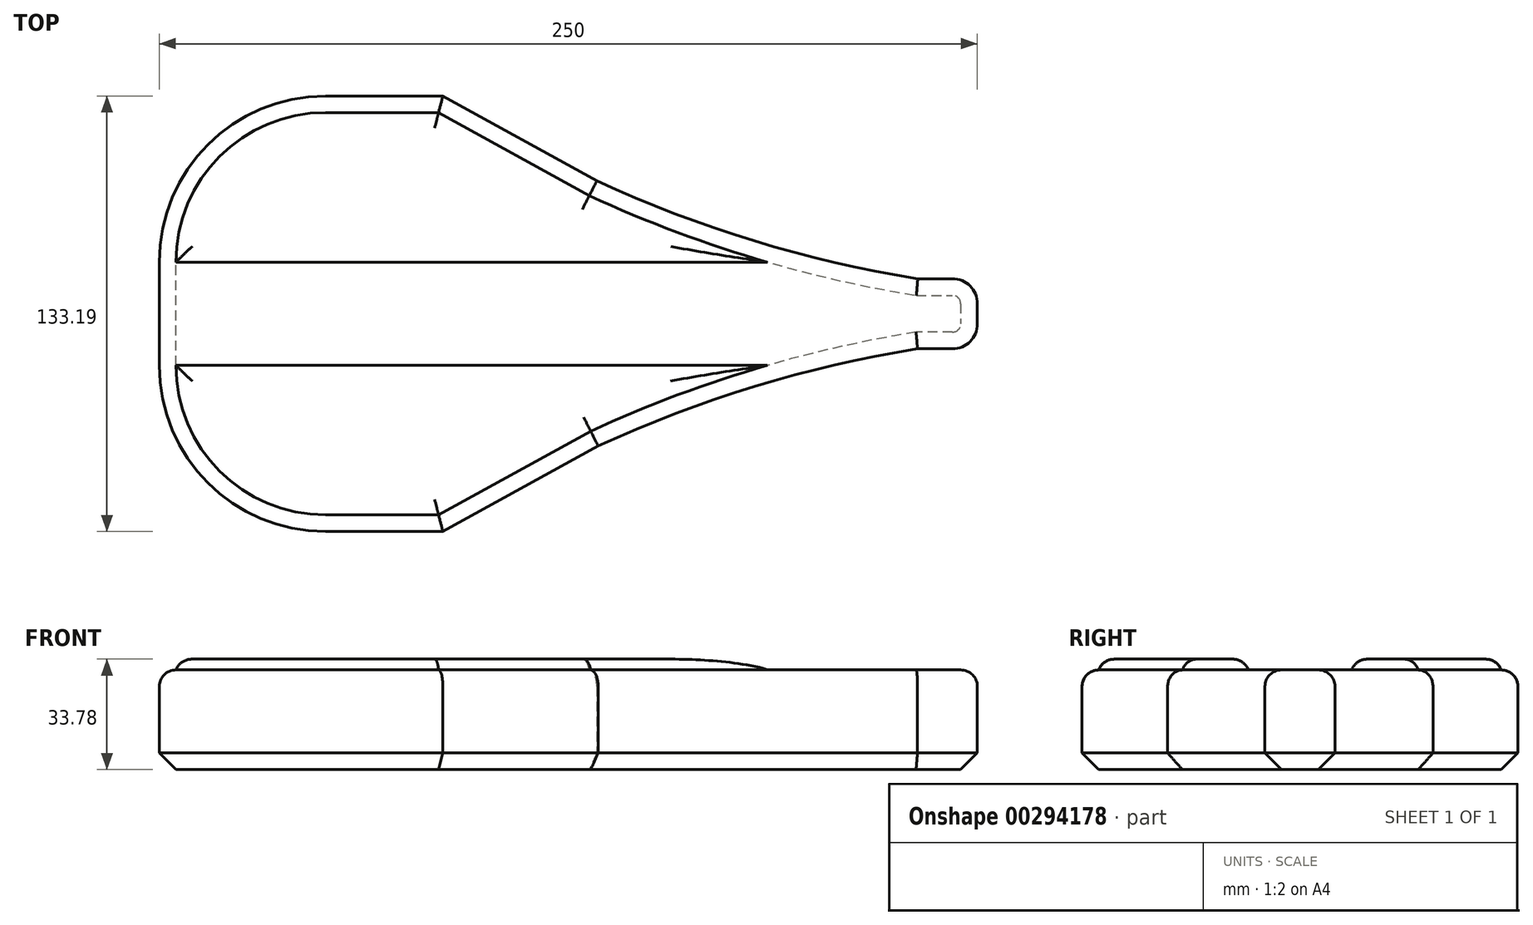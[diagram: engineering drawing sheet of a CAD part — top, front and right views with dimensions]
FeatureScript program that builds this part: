
annotation { "Feature Type Name" : "Feature", "Feature Type Description" : "" }
export const myFeature = defineFeature(function(context is Context, id is Id, definition is map)
    precondition{}
    {
        {
            var Q0;
            Q0=qCreatedBy(makeId("Top.planeOp"),FACE);
            var sketch = newSketch(context, id + "F0", { "sketchPlane" : qUnion([Q0])});
            skLineSegment(sketch, "E0.bottom", {"start": v(0, 0) * mm, "end": v(242.38, 0) * mm});
            skLineSegment(sketch, "E0.top", {"start": v(0, 21.4) * mm, "end": v(242.38, 21.4) * mm});
            skLineSegment(sketch, "E0.left", {"start": v(0, 0) * mm, "end": v(0, 21.4) * mm});
            skLineSegment(sketch, "E0.right", {"start": v(250, 7.62) * mm, "end": v(250, 13.78) * mm});
            skLineSegment(sketch, "E1", {"start": v(0, 21.4) * mm, "end": v(0, 26.51) * mm});
            skLineSegment(sketch, "E2", {"start": v(50.8, 77.31) * mm, "end": v(86.67, 77.31) * mm});
            skLineSegment(sketch, "E3", {"start": v(86.67, 77.31) * mm, "end": v(188.03, 21.4) * mm});
            skLineSegment(sketch, "E4", {"start": v(0, 0) * mm, "end": v(0, -5.08) * mm});
            skLineSegment(sketch, "E5", {"start": v(50.8, -55.88) * mm, "end": v(86.67, -55.88) * mm});
            skLineSegment(sketch, "E6", {"start": v(86.67, -55.88) * mm, "end": v(188.03, 0) * mm});
            skLineSegment(sketch, "E7", {"start": v(534.33, 84.19) * mm, "end": v(534.33, -26.78) * mm});
            skLineSegment(sketch, "E8", {"start": v(561.26, -52.14) * mm, "end": v(716.71, -42.77) * mm});
            skPoint(sketch, "E9.visualSharp", {"position": v(534.33, -53.76) * mm});
            skArc(sketch, "E9.filletArc", {"start": v(534.33, -26.78) * mm, "mid": v(542.32, -45.27) * mm, "end": v(561.26, -52.14) * mm});
            skPoint(sketch, "E10.visualSharp", {"position": v(0, 77.31) * mm});
            skArc(sketch, "E10.filletArc", {"start": v(50.8, 77.31) * mm, "mid": v(14.88, 62.43) * mm, "end": v(0, 26.51) * mm});
            skPoint(sketch, "E11.visualSharp", {"position": v(0, -55.88) * mm});
            skArc(sketch, "E11.filletArc", {"start": v(0, -5.08) * mm, "mid": v(14.88, -41) * mm, "end": v(50.8, -55.88) * mm});
            skLineSegment(sketch, "E12", {"start": v(543.07, 91.73) * mm, "end": v(556.65, 89.7) * mm});
            skPoint(sketch, "E13.visualSharp", {"position": v(534.33, 93.03) * mm});
            skArc(sketch, "E13.filletArc", {"start": v(543.07, 91.73) * mm, "mid": v(536.98, 89.96) * mm, "end": v(534.33, 84.19) * mm});
            skPoint(sketch, "E14.visualSharp", {"position": v(250, 21.4) * mm});
            skArc(sketch, "E14.filletArc", {"start": v(250, 13.78) * mm, "mid": v(247.77, 19.17) * mm, "end": v(242.38, 21.4) * mm});
            skPoint(sketch, "E15.visualSharp", {"position": v(250, 0) * mm});
            skArc(sketch, "E15.filletArc", {"start": v(242.38, 0) * mm, "mid": v(247.77, 2.23) * mm, "end": v(250, 7.62) * mm});
            skArc(sketch, "E16", {"start": v(86.67, 77.31) * mm, "mid": v(163.88, 38.98) * mm, "end": v(247.77, 19.17) * mm});
            skArc(sketch, "E17", {"start": v(247.77, 2.23) * mm, "mid": v(163.87, -17.53) * mm, "end": v(86.67, -55.88) * mm});
            skSolve(sketch);
        }
        {
            var Q0;
            Q0 = qSketchRegion(id + "F0", true);
            extrude(context, id + "F1", {"entities" : qUnion([Q0]), "depth" : 30.48 * mm});
        }
        {
            var Q0;
            Q0=makeQuery(id+"F1.opExtrude","CAP_FACE",FACE,{"disambiguationData":[OSD([sQuery(id+"F0.wireOp",EDGE,"E0.bottom"),sQuery(id+"F0.wireOp",EDGE,"E0.top"),sQuery(id+"F0.wireOp",EDGE,"E0.left"),sQuery(id+"F0.wireOp",EDGE,"E0.right"),sQuery(id+"F0.wireOp",EDGE,"E1"),sQuery(id+"F0.wireOp",EDGE,"E2"),sQuery(id+"F0.wireOp",EDGE,"E3"),sQuery(id+"F0.wireOp",EDGE,"E4"),sQuery(id+"F0.wireOp",EDGE,"E5"),sQuery(id+"F0.wireOp",EDGE,"E6"),sQuery(id+"F0.wireOp",EDGE,"E10.filletArc"),sQuery(id+"F0.wireOp",EDGE,"E11.filletArc"),sQuery(id+"F0.wireOp",EDGE,"E14.filletArc"),sQuery(id+"F0.wireOp",EDGE,"E15.filletArc"),sQuery(id+"F0.wireOp",EDGE,"E16"),sQuery(id+"F0.wireOp",EDGE,"E17")])],"isStart":false});
            fillet(context, id + "F2", {"entities" : qUnion([Q0]), "radius" : 5.08 * mm, "tangentPropagation" : true, "allowEdgeOverflow" : false});
        }
        {
            var Q0;
            Q0=makeQuery(id+"F1.opExtrude","CAP_FACE",FACE,{"disambiguationData":[OSD([sQuery(id+"F0.wireOp",EDGE,"E0.bottom"),sQuery(id+"F0.wireOp",EDGE,"E0.top"),sQuery(id+"F0.wireOp",EDGE,"E0.left"),sQuery(id+"F0.wireOp",EDGE,"E0.right"),sQuery(id+"F0.wireOp",EDGE,"E1"),sQuery(id+"F0.wireOp",EDGE,"E2"),sQuery(id+"F0.wireOp",EDGE,"E3"),sQuery(id+"F0.wireOp",EDGE,"E4"),sQuery(id+"F0.wireOp",EDGE,"E5"),sQuery(id+"F0.wireOp",EDGE,"E6"),sQuery(id+"F0.wireOp",EDGE,"E10.filletArc"),sQuery(id+"F0.wireOp",EDGE,"E11.filletArc"),sQuery(id+"F0.wireOp",EDGE,"E14.filletArc"),sQuery(id+"F0.wireOp",EDGE,"E15.filletArc"),sQuery(id+"F0.wireOp",EDGE,"E16"),sQuery(id+"F0.wireOp",EDGE,"E17")])],"isStart":true});
            chamfer(context, id + "F3", {"entities" : qUnion([Q0]), "width" : 5.08 * mm, "tangentPropagation" : true});
        }
        {
            var Q0;
            Q0=makeQuery(id+"F1.opExtrude","CAP_FACE",FACE,{"disambiguationData":[OSD([sQuery(id+"F0.wireOp",EDGE,"E0.bottom"),sQuery(id+"F0.wireOp",EDGE,"E0.top"),sQuery(id+"F0.wireOp",EDGE,"E0.left"),sQuery(id+"F0.wireOp",EDGE,"E0.right"),sQuery(id+"F0.wireOp",EDGE,"E1"),sQuery(id+"F0.wireOp",EDGE,"E2"),sQuery(id+"F0.wireOp",EDGE,"E3"),sQuery(id+"F0.wireOp",EDGE,"E4"),sQuery(id+"F0.wireOp",EDGE,"E5"),sQuery(id+"F0.wireOp",EDGE,"E6"),sQuery(id+"F0.wireOp",EDGE,"E10.filletArc"),sQuery(id+"F0.wireOp",EDGE,"E11.filletArc"),sQuery(id+"F0.wireOp",EDGE,"E14.filletArc"),sQuery(id+"F0.wireOp",EDGE,"E15.filletArc"),sQuery(id+"F0.wireOp",EDGE,"E16"),sQuery(id+"F0.wireOp",EDGE,"E17")])],"isStart":false});
            var sketch = newSketch(context, id + "F4", { "sketchPlane" : qUnion([Q0])});
            skLineSegment(sketch, "E18", {"start": v(5.08, -5.08) * mm, "end": v(185.8, -5.08) * mm});
            skLineSegment(sketch, "E19", {"start": v(5.08, 26.51) * mm, "end": v(185.85, 26.51) * mm});
            skSolve(sketch);
        }
        {
            var Q0;
            Q0 = qSketchRegion(id + "F4", true);
            var Q1;
            {var subQ6=sQuery(id+"F4.wireOp",EDGE,"E19");Q1=makeQuery(id+"F4.imprint","IMPRINT",FACE,{"disambiguationData":[TD([[makeQuery(id+"F4.imprint","IMPRINT",EDGE,{"derivedFrom":subQ6}),1.0]])]});}
            var Q2;
            {var subQ5=sQuery(id+"F4.wireOp",EDGE,"E18");Q2=makeQuery(id+"F4.imprint","IMPRINT",FACE,{"disambiguationData":[TD([[makeQuery(id+"F4.imprint","IMPRINT",EDGE,{"derivedFrom":subQ5}),-1.0]])]});}
            extrude(context, id + "F5", {"entities" : qUnion([Q0, Q1, Q2]), "operationType" : NewBodyOperationType.ADD, "depth" : 3.3 * mm});
        }
        {
            var Q0;
            Q0=makeQuery(id+"F5.opExtrude","CAP_FACE",FACE,{"disambiguationData":[OSD([sQuery(id+"F0.wireOp",EDGE,"E0.bottom"),sQuery(id+"F0.wireOp",EDGE,"E0.top"),sQuery(id+"F0.wireOp",EDGE,"E0.left"),sQuery(id+"F0.wireOp",EDGE,"E0.right"),sQuery(id+"F0.wireOp",EDGE,"E1"),sQuery(id+"F0.wireOp",EDGE,"E2"),sQuery(id+"F0.wireOp",EDGE,"E3"),sQuery(id+"F0.wireOp",EDGE,"E4"),sQuery(id+"F0.wireOp",EDGE,"E5"),sQuery(id+"F0.wireOp",EDGE,"E6"),sQuery(id+"F0.wireOp",EDGE,"E10.filletArc"),sQuery(id+"F0.wireOp",EDGE,"E11.filletArc"),sQuery(id+"F0.wireOp",EDGE,"E14.filletArc"),sQuery(id+"F0.wireOp",EDGE,"E15.filletArc"),sQuery(id+"F0.wireOp",EDGE,"E16"),sQuery(id+"F0.wireOp",EDGE,"E17"),sQuery(id+"F4.wireOp",EDGE,"E19")])],"isStart":false});
            var Q1;
            Q1=makeQuery(id+"F5.opExtrude","CAP_FACE",FACE,{"disambiguationData":[OSD([sQuery(id+"F0.wireOp",EDGE,"E0.bottom"),sQuery(id+"F0.wireOp",EDGE,"E0.top"),sQuery(id+"F0.wireOp",EDGE,"E0.left"),sQuery(id+"F0.wireOp",EDGE,"E0.right"),sQuery(id+"F0.wireOp",EDGE,"E1"),sQuery(id+"F0.wireOp",EDGE,"E2"),sQuery(id+"F0.wireOp",EDGE,"E3"),sQuery(id+"F0.wireOp",EDGE,"E4"),sQuery(id+"F0.wireOp",EDGE,"E5"),sQuery(id+"F0.wireOp",EDGE,"E6"),sQuery(id+"F0.wireOp",EDGE,"E10.filletArc"),sQuery(id+"F0.wireOp",EDGE,"E11.filletArc"),sQuery(id+"F0.wireOp",EDGE,"E14.filletArc"),sQuery(id+"F0.wireOp",EDGE,"E15.filletArc"),sQuery(id+"F0.wireOp",EDGE,"E16"),sQuery(id+"F0.wireOp",EDGE,"E17"),sQuery(id+"F4.wireOp",EDGE,"E18")])],"isStart":false});
            fillet(context, id + "F6", {"entities" : qUnion([Q0, Q1]), "radius" : 5.08 * mm, "tangentPropagation" : true, "allowEdgeOverflow" : false});
        }
    });
